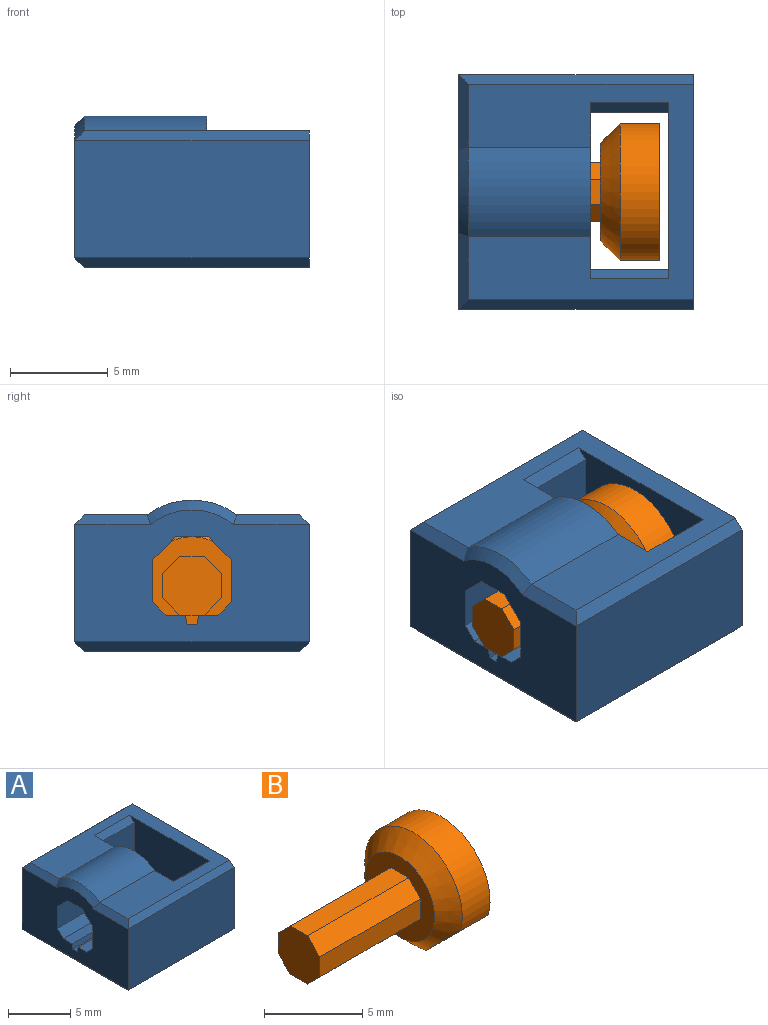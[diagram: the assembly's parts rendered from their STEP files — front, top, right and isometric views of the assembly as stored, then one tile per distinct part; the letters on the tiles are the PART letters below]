
ASSEMBLY  parts=2 mates=1
PART A: 37 faces, bbox 12x12x7.8 mm
  f0: plane 12x6.75mm, normal (-1,0,0), area 59.7mm2, adj f1,f2,f7,f8,f9,f10,f11,f12
  f1: plane 12x6mm, normal (0,1,0), area 72mm2, adj f0,f3,f27,f33
  f2: plane 12x6mm, normal (0,-1,0), area 72mm2, adj f0,f3,f29,f32
  f3: plane 12x7mm, normal (1,0,0), area 83.5mm2, adj f1,f2,f4,f5,f27,f29,f32,f33
  f4: plane 11.5x11mm, normal (0,0,1), area 61.9mm2, adj f3,f6,f19,f22,f27,f28,f29,f31
  f5: plane 11.5x11mm, normal (0,0,-1), area 81.5mm2, adj f3,f23,f24,f25,f26,f32,f33,f34
  f6: cylinder r=3.88mm len=6.25mm, axis (-1,0,0), area 30.6mm2, adj f4,f19,f30
  f7: plane 6.75x1.66mm, normal (0,0,-1), area 11.2mm2, adj f0,f8,f18,f19
  f8: plane 6.75x1.17mm, normal (0,-0.71,-0.71), area 11.2mm2, adj f0,f7,f9,f19
  f9: plane 6.75x2.16mm, normal (0,-1,0), area 14.6mm2, adj f0,f8,f10,f19
  f10: plane 6.75x0.67mm, normal (0,-0.71,0.71), area 6.4mm2, adj f0,f9,f11,f19
  f11: plane 6.75x0.99mm, normal (0,0,1), area 6.7mm2, adj f0,f10,f12,f19
  f12: plane 6.75x0.5mm, normal (0,-0.98,0.17), area 3.4mm2, adj f0,f11,f13,f19
  f13: plane 6.75x0.51mm, normal (0,0,1), area 3.4mm2, adj f0,f12,f14,f19
  f14: plane 6.75x0.5mm, normal (0,0.98,0.17), area 3.4mm2, adj f0,f13,f15,f19
  f15: plane 6.75x0.99mm, normal (0,0,1), area 6.7mm2, adj f0,f14,f16,f19
  f16: plane 6.75x0.67mm, normal (0,0.71,0.71), area 6.4mm2, adj f0,f15,f17,f19
  f17: plane 6.75x2.16mm, normal (0,1,0), area 14.6mm2, adj f0,f16,f18,f19
  f18: plane 6.75x1.17mm, normal (0,0.71,-0.71), area 11.2mm2, adj f0,f7,f17,f19
  f19: plane 9x7.25mm, normal (1,0,0), area 40.1mm2, adj f4,f6,f7,f8,f9,f10,f11,f12
  f20: plane 6x4mm, normal (0,1,0), area 24mm2, adj f19,f22,f24,f35
  f21: plane 6x4mm, normal (0,-1,0), area 24mm2, adj f19,f22,f25,f36
  f22: plane 9x6.5mm, normal (-1,0,0), area 52.3mm2, adj f4,f20,f21,f23,f35,f36
  f23: plane 9x0.5mm, normal (-0.71,0,-0.71), area 6mm2, adj f5,f22,f24,f25
  f24: plane 5x0.5mm, normal (0,0.71,-0.71), area 3.2mm2, adj f5,f20,f23,f26
  f25: plane 5x0.5mm, normal (0,-0.71,-0.71), area 3.2mm2, adj f5,f21,f23,f26
  f26: plane 9x0.5mm, normal (0.71,0,-0.71), area 6mm2, adj f5,f19,f24,f25
  f27: plane 12x0.5mm, normal (0,0.71,0.71), area 8.3mm2, adj f1,f3,f4,f28
  f28: plane 3.89x0.51mm, normal (-0.71,0,0.71), area 2.5mm2, adj f0,f4,f27,f30
  f29: plane 12x0.5mm, normal (0,-0.71,0.71), area 8.3mm2, adj f2,f3,f4,f31
  f30: cone r=3.38mm half-angle=45deg, axis (1,0,0), area 3.4mm2, adj f0,f6,f28,f31
  f31: plane 3.89x0.51mm, normal (-0.71,0,0.71), area 2.5mm2, adj f0,f4,f29,f30
  f32: plane 12x0.5mm, normal (0,-0.71,-0.71), area 8.3mm2, adj f2,f3,f5,f34
  f33: plane 12x0.5mm, normal (0,0.71,-0.71), area 8.3mm2, adj f1,f3,f5,f34
  f34: plane 12x0.5mm, normal (-0.71,0,-0.71), area 8.1mm2, adj f0,f5,f32,f33
  f35: plane 4x0.5mm, normal (0,0.71,0.71), area 2.8mm2, adj f4,f19,f20,f22
  f36: plane 4x0.5mm, normal (0,-0.71,0.71), area 2.8mm2, adj f4,f19,f21,f22
PART B: 38 faces, bbox 10.3x7x7 mm
  f0: plane 1.75x0.88mm, normal (0,0.71,-0.71), area 1.6mm2, adj f5,f18,f32,f35
  f1: plane 1.25x0.88mm, normal (0,0.71,-0.71), area 1.2mm2, adj f4,f14,f18,f37
  f2: plane 1.75x0.88mm, normal (0,0.71,-0.71), area 1.6mm2, adj f6,f18,f29,f33
  f3: plane 1x0.88mm, normal (0,0.71,-0.71), area 0.9mm2, adj f18,f19,f21,f30
  f4: plane 1.24x0.75mm, normal (0,0,-1), area 0.9mm2, adj f1,f8,f14,f37
  f5: plane 1.24x0.75mm, normal (0,0,-1), area 0.9mm2, adj f0,f7,f32,f35
  f6: plane 1.24x0.75mm, normal (0,0,-1), area 0.9mm2, adj f2,f9,f29,f33
  f7: plane 1.75x0.88mm, normal (0,-0.71,-0.71), area 1.6mm2, adj f5,f20,f32,f35
  f8: plane 1.25x0.88mm, normal (0,-0.71,-0.71), area 1.2mm2, adj f4,f14,f20,f37
  f9: plane 1.75x0.88mm, normal (0,-0.71,-0.71), area 1.6mm2, adj f6,f20,f29,f33
  f10: plane 1x0.88mm, normal (0,-0.71,-0.71), area 0.9mm2, adj f19,f20,f21,f30
  f11: cylinder r=3.5mm len=7mm, axis (1,0,0), area 25.7mm2, adj f12,f13,f23,f24
  f12: plane 7x6.88mm, normal (1,0,0), area 35.8mm2, adj f11,f22,f23,f24,f25,f26,f27,f28
  f13: cone r=3.5mm half-angle=45deg, axis (1,0,0), area 22.9mm2, adj f11,f14,f22,f23,f24,f25,f26,f27
  f14: plane 5x5mm, normal (-1,0,0), area 12.2mm2, adj f1,f4,f8,f13,f15,f16,f17,f18
  f15: plane 7.25x0.88mm, normal (0,-0.71,0.71), area 9mm2, adj f14,f16,f20,f21
  f16: plane 7.25x1.24mm, normal (0,0,1), area 9mm2, adj f14,f15,f17,f21
  f17: plane 7.25x0.88mm, normal (0,0.71,0.71), area 9mm2, adj f14,f16,f18,f21
  f18: plane 7.25x1.24mm, normal (0,1,0), area 9mm2, adj f0,f1,f2,f3,f14,f17,f21,f31
  f19: plane 1.24x0.5mm, normal (0,0,-1), area 0.6mm2, adj f3,f10,f21,f30
  f20: plane 7.25x1.24mm, normal (0,-1,0), area 9mm2, adj f7,f8,f9,f10,f14,f15,f21,f31
  f21: plane 3x3mm, normal (-1,0,0), area 7.5mm2, adj f3,f10,f15,f16,f17,f18,f19,f20
  f22: plane 2.12x0.53mm, normal (0,0,-1), area 1mm2, adj f12,f13,f23,f28
  f23: plane 2.46x2.45mm, normal (0,-0.71,-0.71), area 8mm2, adj f11,f12,f13,f22
  f24: plane 2.46x2.45mm, normal (0,0.71,-0.71), area 8mm2, adj f11,f12,f13,f25
  f25: plane 2.13x0.53mm, normal (0,0,-1), area 1mm2, adj f12,f13,f24,f26
  f26: plane 2.62x0.51mm, normal (0,-0.94,-0.33), area 1.2mm2, adj f12,f13,f25,f27
  f27: plane 2.63x0.51mm, normal (0,0,-1), area 1.3mm2, adj f12,f13,f26,f28
  f28: plane 2.62x0.51mm, normal (0,0.94,-0.33), area 1.2mm2, adj f12,f13,f22,f27
  f29: plane 3x0.88mm, normal (-0.87,0,-0.49), area 2.1mm2, adj f2,f6,f9,f31
  f30: plane 3x0.88mm, normal (0.87,0,-0.49), area 2.1mm2, adj f3,f10,f19,f31
  f31: plane 3x0.5mm, normal (0,0,-1), area 1.5mm2, adj f18,f20,f29,f30
  f32: plane 3x0.88mm, normal (-0.87,0,-0.49), area 2.1mm2, adj f0,f5,f7,f34
  f33: plane 3x0.88mm, normal (0.87,0,-0.49), area 2.1mm2, adj f2,f6,f9,f34
  f34: plane 3x0.5mm, normal (0,0,-1), area 1.5mm2, adj f18,f20,f32,f33
  f35: plane 3x0.88mm, normal (0.87,0,-0.49), area 2.1mm2, adj f0,f5,f7,f36
  f36: plane 3x0.5mm, normal (0,0,-1), area 1.5mm2, adj f18,f20,f35,f37
  f37: plane 3x0.88mm, normal (-0.87,0,-0.49), area 2.1mm2, adj f1,f4,f8,f36
PLACE A t=(28.67,20.25,-6.22)mm
PLACE B t=(-12.7,18.83,-2.84)mm
MATE fastened A.f6 <-> B.f21  axis (-1,0,0) through (-14.81,-7.28,-2.34)mm
